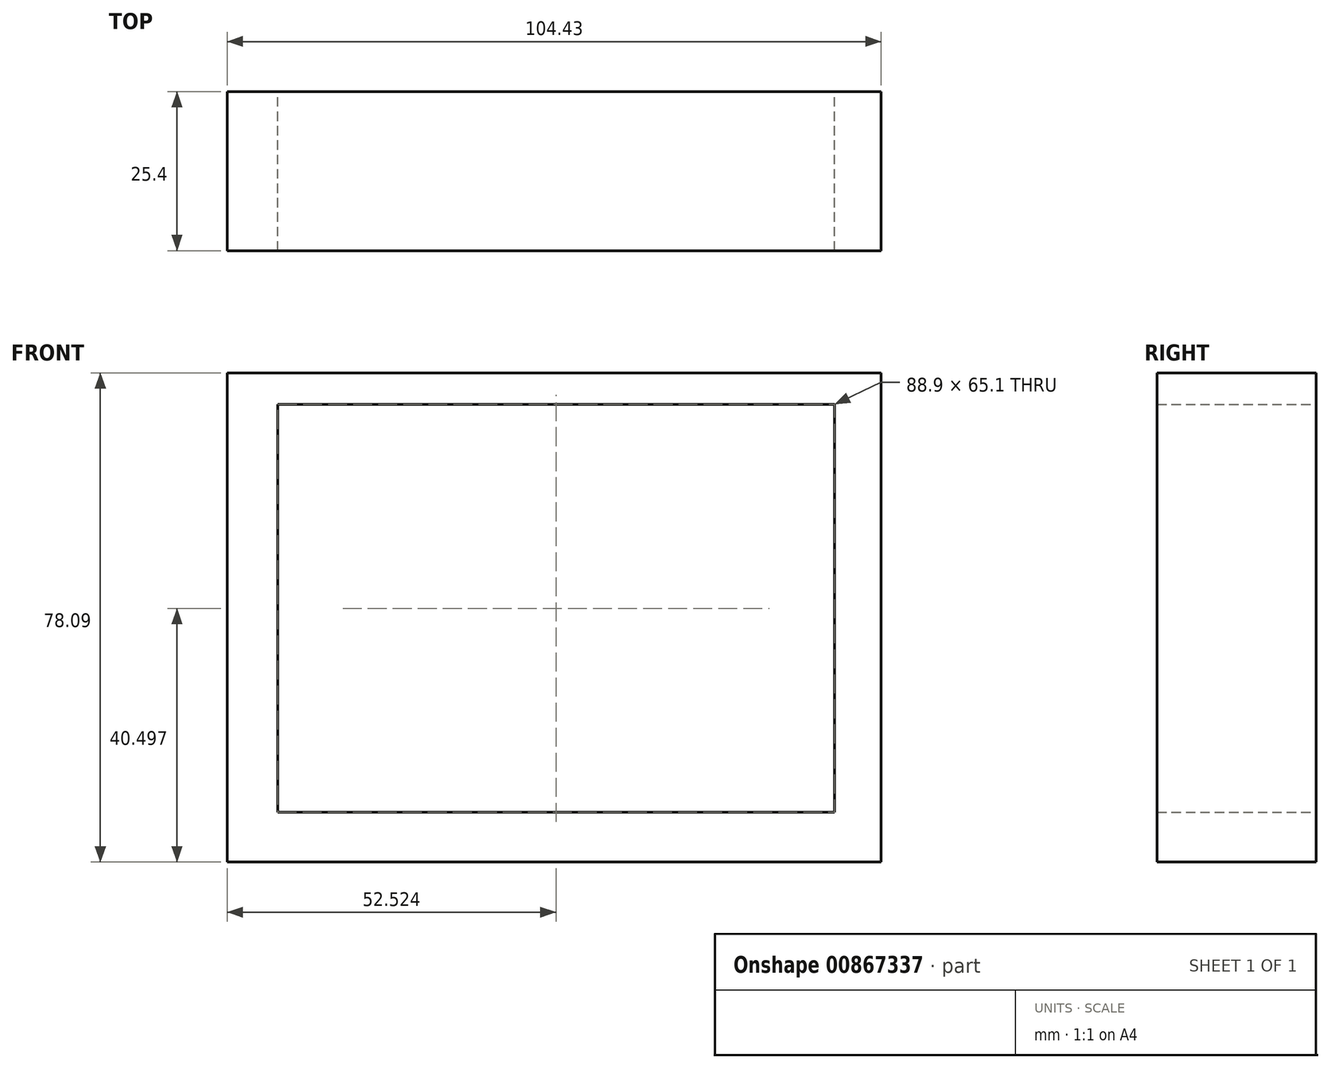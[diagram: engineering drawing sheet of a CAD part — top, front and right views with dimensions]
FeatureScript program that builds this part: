
annotation { "Feature Type Name" : "Feature", "Feature Type Description" : "" }
export const myFeature = defineFeature(function(context is Context, id is Id, definition is map)
    precondition{}
    {
        {
            var Q0;
            Q0=qCreatedBy(makeId("Front.planeOp"),FACE);
            var sketch = newSketch(context, id + "F0", { "sketchPlane" : qUnion([Q0])});
            skLineSegment(sketch, "E0.bottom", {"start": v(-43.74, 63.71) * mm, "end": v(60.69, 63.71) * mm});
            skLineSegment(sketch, "E0.top", {"start": v(-43.74, -14.38) * mm, "end": v(60.69, -14.38) * mm});
            skLineSegment(sketch, "E0.left", {"start": v(-43.74, 63.71) * mm, "end": v(-43.74, -14.38) * mm});
            skLineSegment(sketch, "E0.right", {"start": v(60.69, 63.71) * mm, "end": v(60.69, -14.38) * mm});
            skLineSegment(sketch, "E1.bottom", {"start": v(-35.67, 58.67) * mm, "end": v(53.24, 58.67) * mm});
            skLineSegment(sketch, "E1.top", {"start": v(-35.67, -6.43) * mm, "end": v(53.24, -6.43) * mm});
            skLineSegment(sketch, "E1.left", {"start": v(-35.67, 58.67) * mm, "end": v(-35.67, -6.43) * mm});
            skLineSegment(sketch, "E1.right", {"start": v(53.24, 58.67) * mm, "end": v(53.24, -6.43) * mm});
            skSolve(sketch);
        }
        {
            var Q0;
            Q0 = qSketchRegion(id + "F0", true);
            extrude(context, id + "F1", {"entities" : qUnion([Q0]), "depth" : 25.4 * mm, "offsetDistance" : 25.4 * mm});
        }
    });
